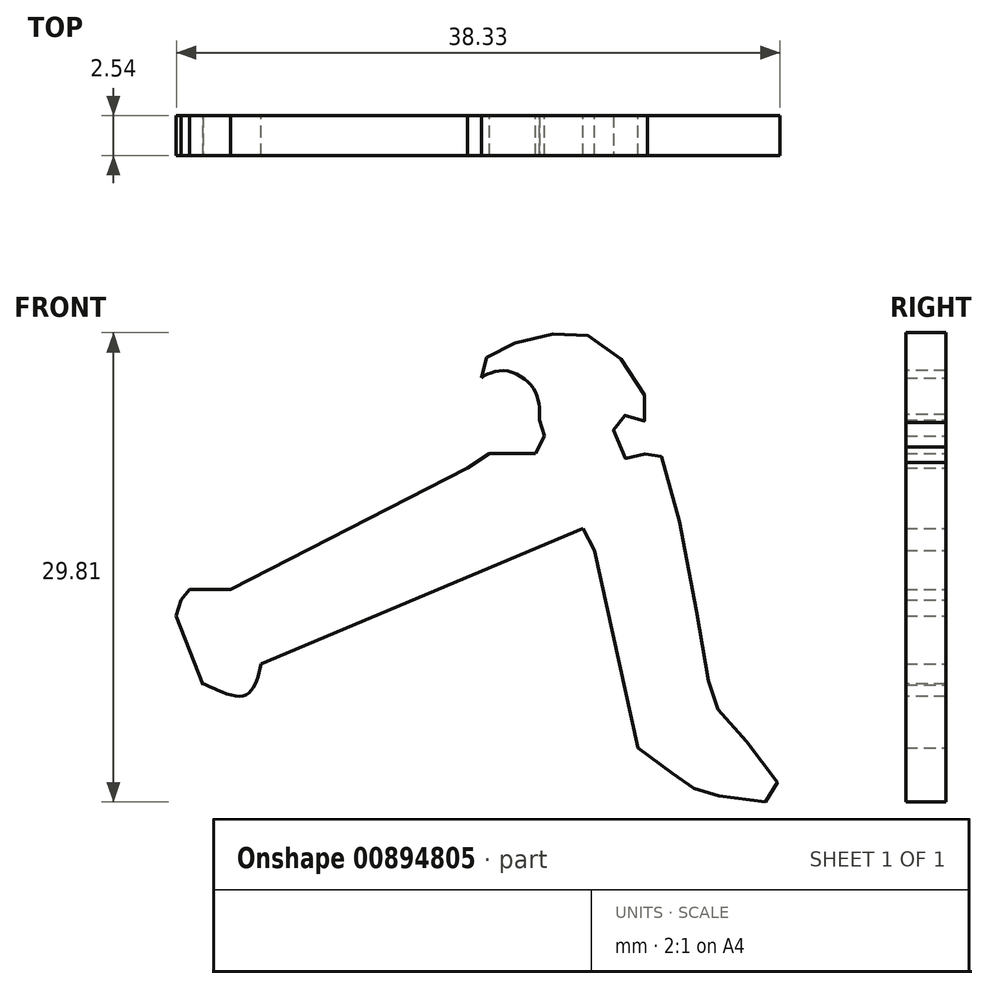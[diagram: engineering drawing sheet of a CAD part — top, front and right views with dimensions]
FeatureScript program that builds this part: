
annotation { "Feature Type Name" : "Feature", "Feature Type Description" : "" }
export const myFeature = defineFeature(function(context is Context, id is Id, definition is map)
    precondition{}
    {
        {
            var Q0;
            Q0=qCreatedBy(makeId("Front.planeOp"),FACE);
            var sketch = newSketch(context, id + "F0", { "sketchPlane" : qUnion([Q0])});
            skLineSegment(sketch, "E0", {"start": v(36.38, 16.1) * mm, "end": v(36.68, 17.12) * mm});
            skLineSegment(sketch, "E1", {"start": v(36.68, 17.12) * mm, "end": v(37.2, 17.8) * mm});
            skLineSegment(sketch, "E2", {"start": v(37.2, 17.8) * mm, "end": v(39.83, 17.8) * mm});
            skLineSegment(sketch, "E3", {"start": v(39.83, 17.8) * mm, "end": v(54.86, 25.52) * mm});
            skLineSegment(sketch, "E4", {"start": v(54.86, 25.52) * mm, "end": v(56.27, 26.45) * mm});
            skLineSegment(sketch, "E5", {"start": v(56.27, 26.45) * mm, "end": v(59.19, 26.45) * mm});
            skLineSegment(sketch, "E6", {"start": v(59.19, 26.45) * mm, "end": v(59.76, 27.53) * mm});
            skLineSegment(sketch, "E7", {"start": v(59.76, 27.53) * mm, "end": v(59.44, 28.56) * mm});
            skFitSpline(sketch, "E8", {"points": [v(59.44, 28.56) * mm, v(59.07, 30.55) * mm, v(56.99, 31.7) * mm, v(55.76, 31.22) * mm, v(55.76, 31.18) * mm], "startDerivative": vector(0.06, 6.33) * mm, "endDerivative": vector(0.34, -0.72) * mm});
            skFitSpline(sketch, "E9", {"points": [v(55.76, 31.22) * mm, v(56.07, 32.52) * mm, v(59.45, 33.87) * mm, v(63.2, 33.62) * mm, v(66.26, 29.61) * mm, v(65.9, 28.41) * mm, v(64.59, 28.89) * mm, v(64.26, 27.2) * mm, v(65.62, 25.9) * mm, v(66.73, 26.83) * mm, v(70.14, 12.2) * mm, v(71.3, 9.56) * mm, v(74.64, 4.65) * mm, v(70.02, 4.88) * mm, v(69.02, 5.3) * mm, v(65.7, 7.75) * mm], "startDerivative": vector(-0.78, 31.64) * mm, "endDerivative": vector(-53.33, 40.14) * mm});
            skLineSegment(sketch, "E10", {"start": v(65.7, 7.75) * mm, "end": v(62.94, 20.26) * mm});
            skLineSegment(sketch, "E11", {"start": v(62.94, 20.26) * mm, "end": v(62.21, 21.68) * mm});
            skLineSegment(sketch, "E12", {"start": v(62.21, 21.68) * mm, "end": v(41.77, 13.07) * mm});
            skFitSpline(sketch, "E13", {"points": [v(41.77, 13.07) * mm, v(40.48, 11.02) * mm, v(38.09, 11.78) * mm, v(38.09, 11.72) * mm], "startDerivative": vector(-1.54, -6.44) * mm, "endDerivative": vector(0.42, -1.11) * mm});
            skLineSegment(sketch, "E14", {"start": v(36.38, 16.1) * mm, "end": v(38.09, 11.72) * mm});
            skSolve(sketch);
        }
        {
            var Q0;
            Q0=makeQuery(id+"F0.imprint","IMPRINT",FACE,{"disambiguationData":[TD([[makeQuery(id+"F0.imprint","IMPRINT",EDGE,{"derivedFrom":sQuery(id+"F0.wireOp",EDGE,"E0")}),-1.0]])]});
            extrude(context, id + "F1", {"entities" : qUnion([Q0]), "depth" : 2.54 * mm, "offsetDistance" : 25.4 * mm});
        }
        {
            var Q0;
            Q0=makeQuery(id+"F1.opExtrude","CAP_FACE",FACE,{"disambiguationData":[OSD([sQuery(id+"F0.wireOp",EDGE,"E0"),sQuery(id+"F0.wireOp",EDGE,"E1"),sQuery(id+"F0.wireOp",EDGE,"E2"),sQuery(id+"F0.wireOp",EDGE,"E3"),sQuery(id+"F0.wireOp",EDGE,"E4"),sQuery(id+"F0.wireOp",EDGE,"E5"),sQuery(id+"F0.wireOp",EDGE,"E6"),sQuery(id+"F0.wireOp",EDGE,"E7"),sQuery(id+"F0.wireOp",EDGE,"E8"),sQuery(id+"F0.wireOp",EDGE,"E9"),sQuery(id+"F0.wireOp",EDGE,"E10"),sQuery(id+"F0.wireOp",EDGE,"E11"),sQuery(id+"F0.wireOp",EDGE,"E12"),sQuery(id+"F0.wireOp",EDGE,"E13"),sQuery(id+"F0.wireOp",EDGE,"E14")])],"isStart":false});
            extrude(context, id + "F2", {"entities" : qUnion([Q0]), "operationType" : NewBodyOperationType.ADD, "oppositeDirection" : true, "depth" : 2.54 * mm, "offsetDistance" : 25.4 * mm});
        }
    });
